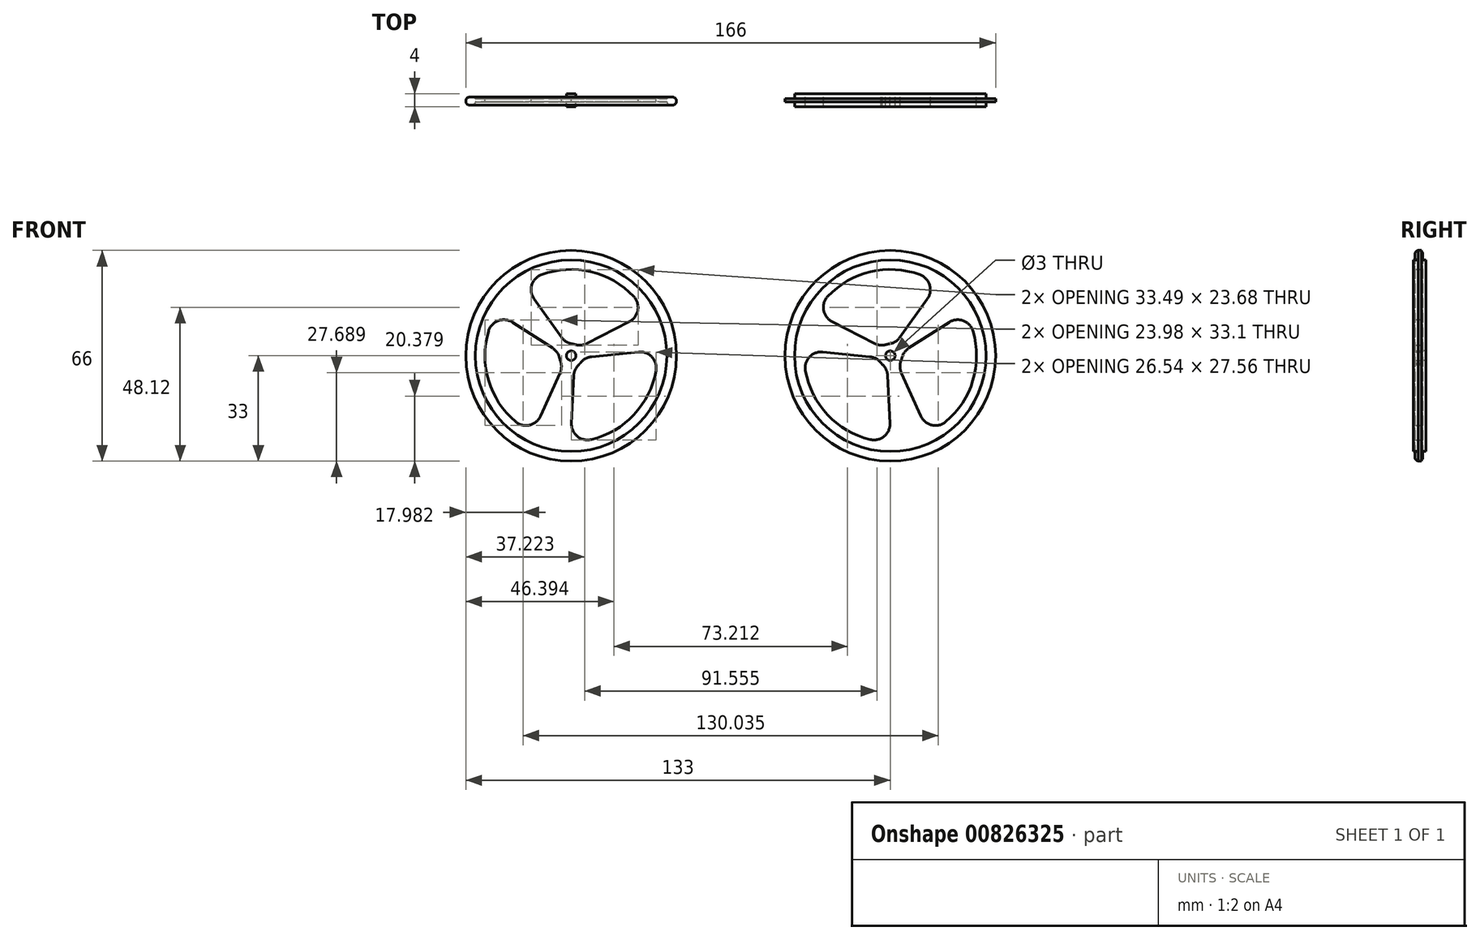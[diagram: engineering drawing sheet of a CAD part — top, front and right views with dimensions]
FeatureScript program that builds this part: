
annotation { "Feature Type Name" : "Feature", "Feature Type Description" : "" }
export const myFeature = defineFeature(function(context is Context, id is Id, definition is map)
    precondition{}
    {
        {
            var Q0;
            Q0=qCreatedBy(makeId("Front.planeOp"),FACE);
            var sketch = newSketch(context, id + "F0", { "sketchPlane" : qUnion([Q0])});
            skCircle(sketch, "E0", {"center": v(0, 0) * mm, "radius": 33 * mm});
            skCircle(sketch, "E1", {"center": v(0, 0) * mm, "radius": 30 * mm});
            skCircle(sketch, "E2", {"center": v(0, 0) * mm, "radius": 1.5 * mm});
            skLineSegment(sketch, "E3.trimOffspring", {"start": v(0, 1.5) * mm, "end": v(0, 0) * mm});
            skPoint(sketch, "E4.start.orphan", {"position": v(0, 30) * mm});
            skLineSegment(sketch, "E5", {"start": v(0, 0) * mm, "end": v(1.5, 0) * mm});
            skCircle(sketch, "E6.MirrorC", {"center": v(100, 0) * mm, "radius": 33 * mm});
            skCircle(sketch, "E7.MirrorC", {"center": v(100, 0) * mm, "radius": 30 * mm});
            skCircle(sketch, "E8.MirrorC", {"center": v(100, 0) * mm, "radius": 1.5 * mm});
            skPoint(sketch, "E9.start.orphan", {"position": v(50, 0) * mm});
            skPoint(sketch, "E10.center.orphan", {"position": v(0, 15) * mm});
            skArc(sketch, "E11", {"start": v(1.13, 3.52) * mm, "mid": v(0.8, 3.6) * mm, "end": v(0.48, 3.67) * mm});
            skArc(sketch, "E12", {"start": v(19.6, 18.57) * mm, "mid": v(6.2, 26.29) * mm, "end": v(-9.24, 25.37) * mm});
            skLineSegment(sketch, "E13", {"start": v(4.95, 3.83) * mm, "end": v(18.26, 10.69) * mm});
            skLineSegment(sketch, "E14", {"start": v(-2.94, 5.71) * mm, "end": v(-11.6, 17.76) * mm});
            skArc(sketch, "E15.filletArc", {"start": v(-9.24, 25.37) * mm, "mid": v(-12.31, 22.15) * mm, "end": v(-11.6, 17.76) * mm});
            skPoint(sketch, "E16.visualSharp", {"position": v(23.47, 13.37) * mm});
            skArc(sketch, "E16.filletArc", {"start": v(18.26, 10.69) * mm, "mid": v(20.9, 14.3) * mm, "end": v(19.6, 18.57) * mm});
            skPoint(sketch, "E17.visualSharp", {"position": v(2.6, 2.63) * mm});
            skArc(sketch, "E17.filletArc", {"start": v(1.13, 3.52) * mm, "mid": v(3.07, 3.3) * mm, "end": v(4.95, 3.83) * mm});
            skPoint(sketch, "E18.visualSharp", {"position": v(-1.32, 3.45) * mm});
            skArc(sketch, "E18.filletArc", {"start": v(-2.94, 5.71) * mm, "mid": v(-1.45, 4.33) * mm, "end": v(0.48, 3.67) * mm});
            skLineSegment(sketch, "E19.1.0", {"start": v(-5.8, 2.37) * mm, "end": v(-18.39, 10.47) * mm});
            skArc(sketch, "E19.1.1", {"start": v(-18.39, 10.47) * mm, "mid": v(-22.83, 10.96) * mm, "end": v(-25.89, 7.7) * mm});
            skArc(sketch, "E19.1.2", {"start": v(-25.89, 7.7) * mm, "mid": v(-25.86, -7.78) * mm, "end": v(-17.35, -20.7) * mm});
            skArc(sketch, "E19.1.3", {"start": v(-17.35, -20.7) * mm, "mid": v(-13.03, -21.74) * mm, "end": v(-9.58, -18.92) * mm});
            skLineSegment(sketch, "E19.1.4", {"start": v(-3.47, -5.4) * mm, "end": v(-9.58, -18.92) * mm});
            skArc(sketch, "E19.1.5", {"start": v(-3.47, -5.4) * mm, "mid": v(-3.03, -3.42) * mm, "end": v(-3.41, -1.42) * mm});
            skArc(sketch, "E19.1.6", {"start": v(-3.61, -0.78) * mm, "mid": v(-3.53, -1.1) * mm, "end": v(-3.41, -1.42) * mm});
            skArc(sketch, "E19.1.7", {"start": v(-3.61, -0.78) * mm, "mid": v(-4.4, 1.01) * mm, "end": v(-5.8, 2.37) * mm});
            skLineSegment(sketch, "E19.2.0", {"start": v(0.84, -6.2) * mm, "end": v(0.12, -21.16) * mm});
            skArc(sketch, "E19.2.1", {"start": v(0.12, -21.16) * mm, "mid": v(1.93, -25.25) * mm, "end": v(6.28, -26.27) * mm});
            skArc(sketch, "E19.2.2", {"start": v(6.28, -26.27) * mm, "mid": v(19.66, -18.5) * mm, "end": v(26.6, -4.68) * mm});
            skArc(sketch, "E19.2.3", {"start": v(26.6, -4.68) * mm, "mid": v(25.34, -0.41) * mm, "end": v(21.18, 1.16) * mm});
            skLineSegment(sketch, "E19.2.4", {"start": v(6.42, -0.3) * mm, "end": v(21.18, 1.16) * mm});
            skArc(sketch, "E19.2.5", {"start": v(6.42, -0.3) * mm, "mid": v(4.48, -0.91) * mm, "end": v(2.94, -2.25) * mm});
            skArc(sketch, "E19.2.6", {"start": v(2.48, -2.74) * mm, "mid": v(2.72, -2.5) * mm, "end": v(2.94, -2.25) * mm});
            skArc(sketch, "E19.2.7", {"start": v(2.48, -2.74) * mm, "mid": v(1.32, -4.31) * mm, "end": v(0.84, -6.2) * mm});
            skLineSegment(sketch, "E20.MirrorCS", {"start": v(95.05, 3.83) * mm, "end": v(81.74, 10.69) * mm});
            skArc(sketch, "E21.MirrorCS", {"start": v(98.87, 3.52) * mm, "mid": v(96.93, 3.3) * mm, "end": v(95.05, 3.83) * mm});
            skArc(sketch, "E22.MirrorCS", {"start": v(98.87, 3.52) * mm, "mid": v(99.2, 3.6) * mm, "end": v(99.52, 3.67) * mm});
            skArc(sketch, "E23.MirrorCS", {"start": v(102.94, 5.71) * mm, "mid": v(101.45, 4.33) * mm, "end": v(99.52, 3.67) * mm});
            skLineSegment(sketch, "E24.MirrorCS", {"start": v(102.94, 5.71) * mm, "end": v(111.6, 17.76) * mm});
            skArc(sketch, "E25.MirrorCS", {"start": v(109.24, 25.37) * mm, "mid": v(112.31, 22.15) * mm, "end": v(111.6, 17.76) * mm});
            skArc(sketch, "E26.MirrorCS", {"start": v(80.4, 18.57) * mm, "mid": v(93.8, 26.29) * mm, "end": v(109.24, 25.37) * mm});
            skArc(sketch, "E27.MirrorCS", {"start": v(81.74, 10.69) * mm, "mid": v(79.1, 14.3) * mm, "end": v(80.4, 18.57) * mm});
            skLineSegment(sketch, "E28.MirrorCS", {"start": v(93.58, -0.3) * mm, "end": v(78.82, 1.16) * mm});
            skArc(sketch, "E29.MirrorCS", {"start": v(93.58, -0.3) * mm, "mid": v(95.52, -0.91) * mm, "end": v(97.06, -2.25) * mm});
            skArc(sketch, "E30.MirrorCS", {"start": v(97.52, -2.74) * mm, "mid": v(98.68, -4.31) * mm, "end": v(99.16, -6.2) * mm});
            skLineSegment(sketch, "E31.MirrorCS", {"start": v(99.16, -6.2) * mm, "end": v(99.88, -21.16) * mm});
            skArc(sketch, "E32.MirrorCS", {"start": v(99.88, -21.16) * mm, "mid": v(98.07, -25.25) * mm, "end": v(93.72, -26.27) * mm});
            skArc(sketch, "E33.MirrorCS", {"start": v(93.72, -26.27) * mm, "mid": v(80.34, -18.5) * mm, "end": v(73.4, -4.68) * mm});
            skArc(sketch, "E34.MirrorCS", {"start": v(73.4, -4.68) * mm, "mid": v(74.66, -0.41) * mm, "end": v(78.82, 1.16) * mm});
            skLineSegment(sketch, "E35.MirrorCS", {"start": v(103.47, -5.4) * mm, "end": v(109.58, -18.92) * mm});
            skArc(sketch, "E36.MirrorCS", {"start": v(117.35, -20.7) * mm, "mid": v(113.03, -21.74) * mm, "end": v(109.58, -18.92) * mm});
            skArc(sketch, "E37.MirrorCS", {"start": v(125.89, 7.7) * mm, "mid": v(125.86, -7.78) * mm, "end": v(117.35, -20.7) * mm});
            skArc(sketch, "E38.MirrorCS", {"start": v(118.39, 10.47) * mm, "mid": v(122.83, 10.96) * mm, "end": v(125.89, 7.7) * mm});
            skLineSegment(sketch, "E39.MirrorCS", {"start": v(105.8, 2.37) * mm, "end": v(118.39, 10.47) * mm});
            skArc(sketch, "E40.MirrorCS", {"start": v(103.61, -0.78) * mm, "mid": v(104.4, 1.01) * mm, "end": v(105.8, 2.37) * mm});
            skArc(sketch, "E41.MirrorCS", {"start": v(103.61, -0.78) * mm, "mid": v(103.53, -1.1) * mm, "end": v(103.41, -1.42) * mm});
            skArc(sketch, "E42.MirrorCS", {"start": v(103.47, -5.4) * mm, "mid": v(103.03, -3.42) * mm, "end": v(103.41, -1.42) * mm});
            skLineSegment(sketch, "E43.trimOffspring", {"start": v(98.5, 0) * mm, "end": v(100, 0) * mm});
            skLineSegment(sketch, "E44", {"start": v(97.06, -2.25) * mm, "end": v(97.52, -2.74) * mm});
            skSolve(sketch);
        }
        {
            var Q0;
            Q0=makeQuery(id+"F0.imprint","IMPRINT",FACE,{"disambiguationData":[TD([[makeQuery(id+"F0.imprint","IMPRINT",EDGE,{"derivedFrom":sQuery(id+"F0.wireOp",EDGE,"E1")}),1.0]])]});
            var Q1;
            Q1=makeQuery(id+"F0.imprint","IMPRINT",FACE,{"disambiguationData":[TD([[makeQuery(id+"F0.imprint","IMPRINT",EDGE,{"derivedFrom":sQuery(id+"F0.wireOp",EDGE,"E7.MirrorC")}),-1.0]])]});
            extrude(context, id + "F1", {"entities" : qUnion([Q0, Q1]), "depth" : 0.5 * mm, "offsetDistance" : 25 * mm});
        }
        {
            var Q0;
            Q0=makeQuery(id+"F0.imprint","IMPRINT",FACE,{"disambiguationData":[TD([[makeQuery(id+"F0.imprint","IMPRINT",EDGE,{"derivedFrom":sQuery(id+"F0.wireOp",EDGE,"E1")}),1.0]])]});
            var Q1;
            Q1=makeQuery(id+"F0.imprint","IMPRINT",FACE,{"disambiguationData":[TD([[makeQuery(id+"F0.imprint","IMPRINT",EDGE,{"derivedFrom":sQuery(id+"F0.wireOp",EDGE,"E7.MirrorC")}),-1.0]])]});
            extrude(context, id + "F2", {"entities" : qUnion([Q0, Q1]), "operationType" : NewBodyOperationType.ADD, "oppositeDirection" : true, "depth" : 0.5 * mm, "offsetDistance" : 25 * mm});
        }
        {
            var Q0;
            Q0=makeQuery(id+"F0.imprint","IMPRINT",FACE,{"disambiguationData":[TD([[makeQuery(id+"F0.imprint","IMPRINT",EDGE,{"derivedFrom":sQuery(id+"F0.wireOp",EDGE,"E0")}),1.0]])]});
            var Q1;
            Q1=makeQuery(id+"F0.imprint","IMPRINT",FACE,{"disambiguationData":[TD([[makeQuery(id+"F0.imprint","IMPRINT",EDGE,{"derivedFrom":sQuery(id+"F0.wireOp",EDGE,"E6.MirrorC")}),-1.0]])]});
            extrude(context, id + "F3", {"entities" : qUnion([Q0, Q1]), "operationType" : NewBodyOperationType.ADD, "depth" : 1.5 * mm, "offsetDistance" : 25 * mm});
        }
        {
            var Q0;
            Q0=makeQuery(id+"F0.imprint","IMPRINT",FACE,{"disambiguationData":[TD([[makeQuery(id+"F0.imprint","IMPRINT",EDGE,{"derivedFrom":sQuery(id+"F0.wireOp",EDGE,"E0")}),1.0]])]});
            var Q1;
            Q1=makeQuery(id+"F0.imprint","IMPRINT",FACE,{"disambiguationData":[TD([[makeQuery(id+"F0.imprint","IMPRINT",EDGE,{"derivedFrom":sQuery(id+"F0.wireOp",EDGE,"E6.MirrorC")}),-1.0]])]});
            extrude(context, id + "F4", {"entities" : qUnion([Q0, Q1]), "operationType" : NewBodyOperationType.ADD, "oppositeDirection" : true, "depth" : 1 * mm, "offsetDistance" : 25 * mm});
        }
        {
            var Q0;
            Q0=makeQuery(id+"F3.opExtrude","CAP_FACE",FACE,{"disambiguationData":[OSD([sQuery(id+"F0.wireOp",EDGE,"E0"),sQuery(id+"F0.wireOp",EDGE,"E1")])],"isStart":false});
            var Q1;
            Q1=makeQuery(id+"F4.opExtrude","CAP_FACE",FACE,{"disambiguationData":[OSD([sQuery(id+"F0.wireOp",EDGE,"E0"),sQuery(id+"F0.wireOp",EDGE,"E1")])],"isStart":false});
            var Q2;
            Q2=makeQuery(id+"F3.opExtrude","CAP_FACE",FACE,{"disambiguationData":[OSD([sQuery(id+"F0.wireOp",EDGE,"E6.MirrorC"),sQuery(id+"F0.wireOp",EDGE,"E7.MirrorC")])],"isStart":false});
            var Q3;
            Q3=makeQuery(id+"F4.opExtrude","CAP_FACE",FACE,{"disambiguationData":[OSD([sQuery(id+"F0.wireOp",EDGE,"E6.MirrorC"),sQuery(id+"F0.wireOp",EDGE,"E7.MirrorC")])],"isStart":false});
            fillet(context, id + "F5", {"entities" : qUnion([Q0, Q1, Q2, Q3]), "radius" : 1.2 * mm, "tangentPropagation" : true, "allowEdgeOverflow" : false});
        }
        {
            var Q0;
            Q0=makeQuery(id+"F0.imprint","IMPRINT",FACE,{"disambiguationData":[TD([[makeQuery(id+"F0.imprint","IMPRINT",EDGE,{"derivedFrom":sQuery(id+"F0.wireOp",EDGE,"E2")}),1.0]])]});
            var Q1;
            Q1=makeQuery(id+"F0.imprint","IMPRINT",FACE,{"disambiguationData":[TD([[makeQuery(id+"F0.imprint","IMPRINT",EDGE,{"derivedFrom":sQuery(id+"F0.wireOp",EDGE,"E8.MirrorC")}),-1.0]])]});
            extrude(context, id + "F6", {"entities" : qUnion([Q0, Q1]), "operationType" : NewBodyOperationType.ADD, "depth" : 2 * mm, "offsetDistance" : 25 * mm});
        }
        {
            var Q0;
            Q0=makeQuery(id+"F0.imprint","IMPRINT",FACE,{"disambiguationData":[TD([[makeQuery(id+"F0.imprint","IMPRINT",EDGE,{"derivedFrom":sQuery(id+"F0.wireOp",EDGE,"E2")}),1.0]])]});
            var Q1;
            Q1=makeQuery(id+"F0.imprint","IMPRINT",FACE,{"disambiguationData":[TD([[makeQuery(id+"F0.imprint","IMPRINT",EDGE,{"derivedFrom":sQuery(id+"F0.wireOp",EDGE,"E8.MirrorC")}),-1.0]])]});
            extrude(context, id + "F7", {"entities" : qUnion([Q0, Q1]), "operationType" : NewBodyOperationType.ADD, "oppositeDirection" : true, "depth" : 2 * mm, "offsetDistance" : 25 * mm});
        }
    });
